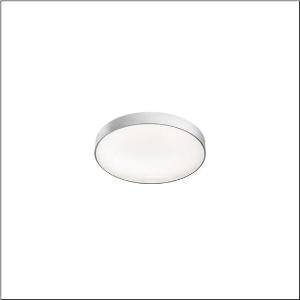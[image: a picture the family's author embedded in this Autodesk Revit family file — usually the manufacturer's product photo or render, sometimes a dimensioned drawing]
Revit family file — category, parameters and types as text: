
# Revit family: round_21_s_51mr34nd0421s
name_source: partatom
category: Lighting Fixtures
units: mm (PartAtom-declared; Revit-internal decimal feet)

## family parameters
Cut with Voids When Loaded = No
Host = Face
Light Source = No
Part Type = Normal
Room Calculation Point = No
Round Connector Dimension = Use Diameter
Shared = No

## types (1)
- Round 21 S (1 x LED, 3810 lm, 28.3 W, 4000K)
    Apparent Load = 28 VA
    CIE Flux Codes = 66 90 98 71 100
    Color Rendering = 80
    Color Temperature = 4000K
    Default Elevation = 1800 mm
    Description = Round 21 S, wall and ceiling luminaire, primary optical cover: micro prismatic cover, of PMMA, transparent, CAT 2 (L<= 3000cd/m²), light emission: direct/indirect distribution, primary light characteristic: symmetric, installation type: surface-mounted, suspended mounting, LED, rated luminous flux: 3.800lm, luminous efficacy: 135lm/W, light colour: 840, colour temperature: 4000K, control gear: DALI 2, with terminal, 5-pole, mains connection: 230V, AC, 50/60Hz, rated input power: 28.3W, housing, of aluminium, coated, silver, diameter: 400mm, height: 62mm, protection rating (complete): IP40, insulation class (complete): insulation class I (protective earthing), certification: CE, impact resistance: IK04, permissible operating ambient temperature: -10..+35°C, packaging unit: 1 piece
    Height = 87 mm
    Lamp = 1 x LED
    Lamp Light Flux = 3810 lm
    Lamp Power = 28.3 W
    Lamp count = 1
    Length = 400 mm
    Luminous efficacy = 135 lm/W
    Manufacturer = Siteco
    ModVariant = No
    Model = 51MR34ND0421S
    Mounting Place = Wall
    Mounting Type = Surface mounted
    Number of Poles = 1
    OnlyDefault = Yes
    Power Factor = 1
    Product Name = Round 21 S
    Product group = wall and ceiling luminaire
    ProductGroupID = 2001
    Protection Class = Protection class I
    Protection Degree = IP 40
    RLX_Detail_Level = 1
    RLX_Emergency_Light_Flux = 0 lm
    RLX_Emergency_Type = 0
    RLX_Emergency_Type_DB = No
    RlxData = <blob elided: 15129 chars, md5=1af0c05c>
    Socket = socket
    Standby Power = 0 W
    System Light Flux = 3810 lm
    System Power = 28 W
    Type Comments = Product without accessories
    Type Image = l_1258336.jpg
    URL = http://relux.com
    VarID = ---
    Voltage = 0 V
    Weight = 0.00 kg
    Width = 0 mm  [stored 0 ft]

note: [stored X ft] marks values corroborated as IEEE doubles in the binary element streams (Revit-internal decimal feet)

## geometry (parser evidence)
native form markers: Sweep x12
no freeform markers — native parametric forms only
